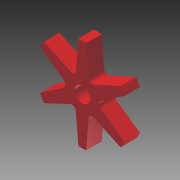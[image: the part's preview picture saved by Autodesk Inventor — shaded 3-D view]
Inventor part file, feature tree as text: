
AUTODESK INVENTOR PART (.ipt)
format: ipt  version: 2012 (Build 160160000, 160)  size: 121,344 bytes
history: native  units: in
note: dims shown in document units (in); Inventor stores cm internally (conversion verified against a paired STEP export)
features: extrude x1, fillet x1, sketch x1
ambient origin geometry x8: Origin, YZ Plane, XZ Plane, XY Plane, X Axis, Y Axis, Z Axis, Center Point
bodies: Solid1 (feature_tree)
feature tree (3):
  extrude  "Extrusion1"  Depth=0.125in
  fillet  "Fillet1"  Radius=0.0344in
  sketch  "Sketch1"  dims[d1=0.25in d2=0.125in d3=0.0344in d4=0.0344in d5=0.0344in d6=0.0344in d7=0.0344in d8=0.0344in d9=0.0344in d10=1.5in d11=0.5in d12=0.0in d13=0.5in d14=0.125in]
